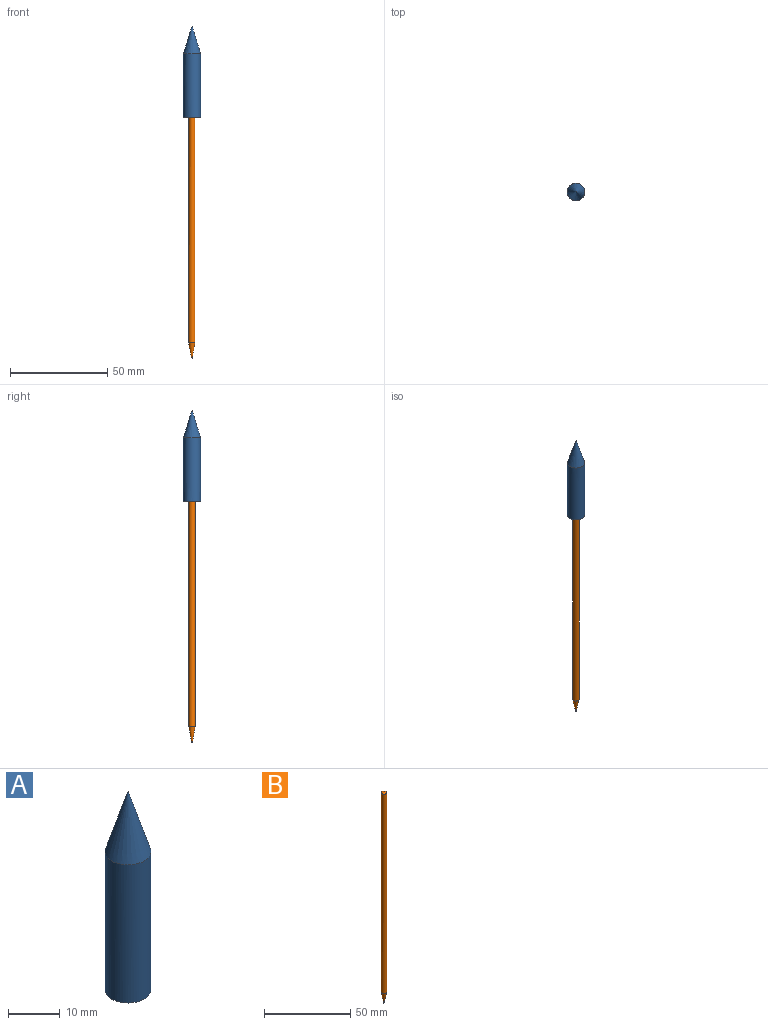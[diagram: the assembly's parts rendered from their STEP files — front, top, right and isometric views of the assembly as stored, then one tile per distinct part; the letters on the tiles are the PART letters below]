
ASSEMBLY  parts=2 mates=1
PART A: 5 faces, bbox 8.9x8.9x46.9 mm
  f0: cylinder r=1.17mm len=4.95mm, axis (0,0,1), area 36.3mm2, adj f1,f4
  f1: plane 2.34x2.34mm, normal (0,0,-1), area 4.3mm2, adj f0
  f2: cone r=4.44mm half-angle=17.2deg, axis (0,0,-1), area 208.9mm2, adj f3
  f3: cylinder r=4.44mm len=32.64mm, axis (0,0,1), area 909.9mm2, adj f2,f4
  f4: plane 8.87x8.87mm, normal (0,0,-1), area 57.6mm2, adj f0,f3
PART B: 4 faces, bbox 3.4x3.3x150 mm
  f0: cone r=0.15mm half-angle=1.1deg, axis (0,0,-1), area 3.8mm2, adj f3
  f1: cone r=0mm half-angle=60.6deg, axis (0,0,-1), area 9.8mm2, adj f2
  f2: cylinder r=1.65mm len=141.36mm, axis (0,0,-1), area 1463.8mm2, adj f1,f3
  f3: cone r=1.65mm half-angle=10.9deg, axis (0,0,1), area 44.7mm2, adj f0,f2
PLACE A rot(axis=(0,1,0),0deg) t=(4.41,-9.04,-58.46)mm
PLACE B t=(14.92,-9.04,-65.5)mm
MATE slider A.f0 <-> B.f0  axis (0,0,-1) through (-22.5,-9.04,-7.08)mm
